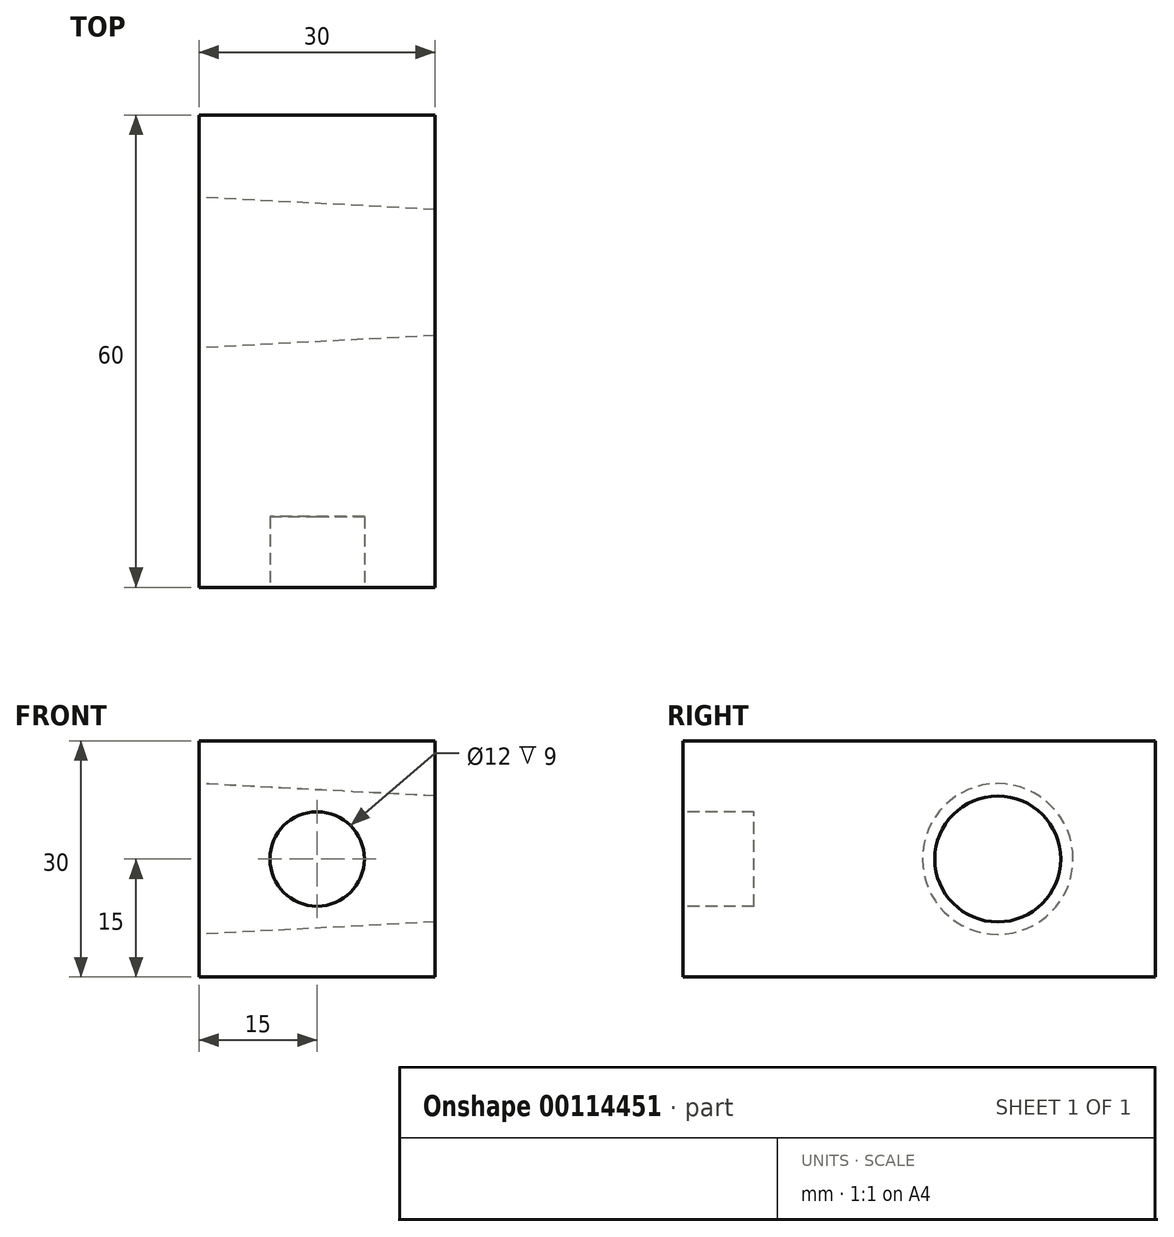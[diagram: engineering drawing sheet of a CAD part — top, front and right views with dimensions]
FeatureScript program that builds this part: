
annotation { "Feature Type Name" : "Feature", "Feature Type Description" : "" }
export const myFeature = defineFeature(function(context is Context, id is Id, definition is map)
    precondition{}
    {
        {
            var Q0;
            Q0=qCreatedBy(makeId("Front.planeOp"),FACE);
            var sketch = newSketch(context, id + "F0", { "sketchPlane" : qUnion([Q0])});
            skLineSegment(sketch, "E0.bottom", {"start": v(15, -15) * mm, "end": v(-15, -15) * mm});
            skLineSegment(sketch, "E0.top", {"start": v(15, 15) * mm, "end": v(-15, 15) * mm});
            skLineSegment(sketch, "E0.left", {"start": v(15, -15) * mm, "end": v(15, 15) * mm});
            skLineSegment(sketch, "E0.right", {"start": v(-15, -15) * mm, "end": v(-15, 15) * mm});
            skPoint(sketch, "E0.middle", {"position": v(0, 0) * mm});
            skSolve(sketch);
        }
        {
            var Q0;
            Q0=makeQuery(id+"F0.imprint","IMPRINT",FACE,{"disambiguationData":[TD([[makeQuery(id+"F0.imprint","IMPRINT",EDGE,{"derivedFrom":sQuery(id+"F0.wireOp",EDGE,"E0.bottom")}),-1.0]])]});
            extrude(context, id + "F1", {"entities" : qUnion([Q0]), "depth" : 60 * mm});
        }
        {
            var Q0;
            Q0=makeQuery(id+"F1.opExtrude","SWEPT_FACE",FACE,{"disambiguationData":[OSD([sQuery(id+"F0.wireOp",EDGE,"E0.left")])]});
            var sketch = newSketch(context, id + "F2", { "sketchPlane" : qUnion([Q0])});
            skCircle(sketch, "E1", {"center": v(-20, 0) * mm, "radius": 8 * mm});
            skSolve(sketch);
        }
        {
            var Q0;
            Q0=makeQuery(id+"F2.imprint","IMPRINT",FACE,{"disambiguationData":[TD([[makeQuery(id+"F2.imprint","IMPRINT",EDGE,{"derivedFrom":sQuery(id+"F2.wireOp",EDGE,"E1")}),1.0]])]});
            extrude(context, id + "F3", {"entities" : qUnion([Q0]), "operationType" : NewBodyOperationType.REMOVE, "endBound" : BoundingType.THROUGH_ALL, "oppositeDirection" : true, "depth" : 25 * mm, "hasDraft" : true, "draftAngle" : 3 * degree});
        }
        {
            var Q0;
            Q0=makeQuery(id+"F1.opExtrude","CAP_FACE",FACE,{"disambiguationData":[OSD([sQuery(id+"F0.wireOp",EDGE,"E0.bottom"),sQuery(id+"F0.wireOp",EDGE,"E0.top"),sQuery(id+"F0.wireOp",EDGE,"E0.left"),sQuery(id+"F0.wireOp",EDGE,"E0.right")])],"isStart":false});
            var sketch = newSketch(context, id + "F4", { "sketchPlane" : qUnion([Q0])});
            skCircle(sketch, "E2", {"center": v(0, 0) * mm, "radius": 6 * mm});
            skSolve(sketch);
        }
        {
            var Q0;
            Q0=makeQuery(id+"F4.imprint","IMPRINT",FACE,{"disambiguationData":[TD([[makeQuery(id+"F4.imprint","IMPRINT",EDGE,{"derivedFrom":sQuery(id+"F4.wireOp",EDGE,"E2")}),1.0]])]});
            extrude(context, id + "F5", {"entities" : qUnion([Q0]), "operationType" : NewBodyOperationType.REMOVE, "oppositeDirection" : true, "depth" : 9 * mm});
        }
    });
